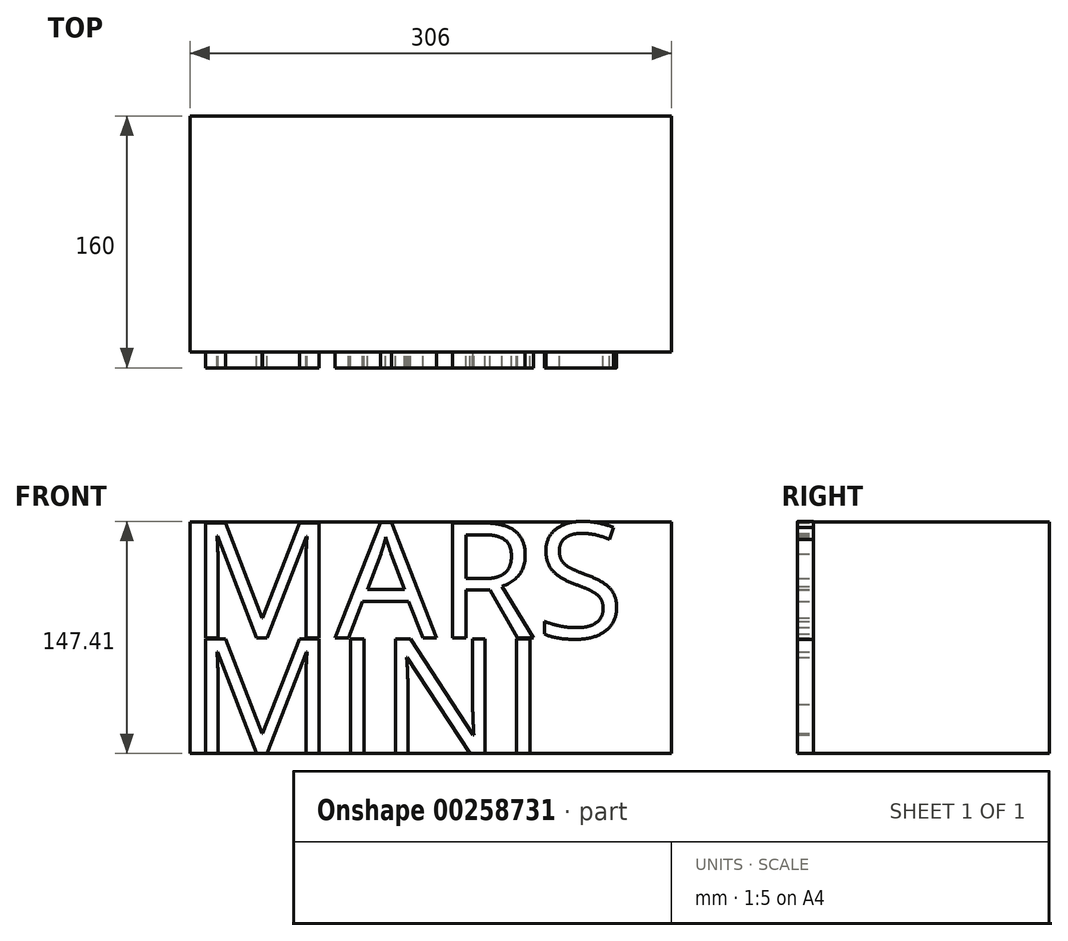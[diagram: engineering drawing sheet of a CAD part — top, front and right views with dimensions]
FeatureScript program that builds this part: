
annotation { "Feature Type Name" : "Feature", "Feature Type Description" : "" }
export const myFeature = defineFeature(function(context is Context, id is Id, definition is map)
    precondition{}
    {
        {
            var Q0;
            Q0=qCreatedBy(makeId("Front.planeOp"),FACE);
            var sketch = newSketch(context, id + "F2", { "sketchPlane" : qUnion([Q0])});
            skLineSegment(sketch, "E0.bottom", {"start": v(0, 0) * mm, "end": v(306, 0) * mm});
            skLineSegment(sketch, "E0.top", {"start": v(0, 147) * mm, "end": v(306, 147) * mm});
            skLineSegment(sketch, "E0.left", {"start": v(0, 0) * mm, "end": v(0, 147) * mm});
            skLineSegment(sketch, "E0.right", {"start": v(306, 0) * mm, "end": v(306, 147) * mm});
            skSolve(sketch);
        }
        {
            var Q0;
            Q0=makeQuery(id+"F2.imprint","IMPRINT",FACE,{"disambiguationData":[TD([[makeQuery(id+"F2.imprint","IMPRINT",EDGE,{"derivedFrom":sQuery(id+"F2.wireOp",EDGE,"E0.bottom")}),1.0]])]});
            extrude(context, id + "F0", {"entities" : qUnion([Q0]), "depth" : 150 * mm});
        }
        {
            var Q0;
            Q0=makeQuery(id+"F0.opExtrude","CAP_FACE",FACE,{"disambiguationData":[OSD([sQuery(id+"F2.wireOp",EDGE,"E0.bottom"),sQuery(id+"F2.wireOp",EDGE,"E0.top"),sQuery(id+"F2.wireOp",EDGE,"E0.left"),sQuery(id+"F2.wireOp",EDGE,"E0.right")])],"isStart":false});
            var sketch = newSketch(context, id + "F1", { "sketchPlane" : qUnion([Q0])});
            skText(sketch, "E1", { "text": "MARS", "fontName": "OpenSans-Regular.ttf"});
            skText(sketch, "E2", { "text": "MINI", "fontName": "OpenSans-Regular.ttf"});
            const initialGuessF1  = {"E1": [0, 0.0735, 1, 0, 0.0735], "E2": [0, 0, 1, 0, 0.0735]};
            skSetInitialGuess(sketch, initialGuessF1);
            skSolve(sketch);
        }
        {
            var Q0;
            Q0 = qSketchRegion(id + "F1", true);
            extrude(context, id + "F3", {"entities" : qUnion([Q0]), "operationType" : NewBodyOperationType.ADD, "depth" : 10 * mm});
        }
    });
